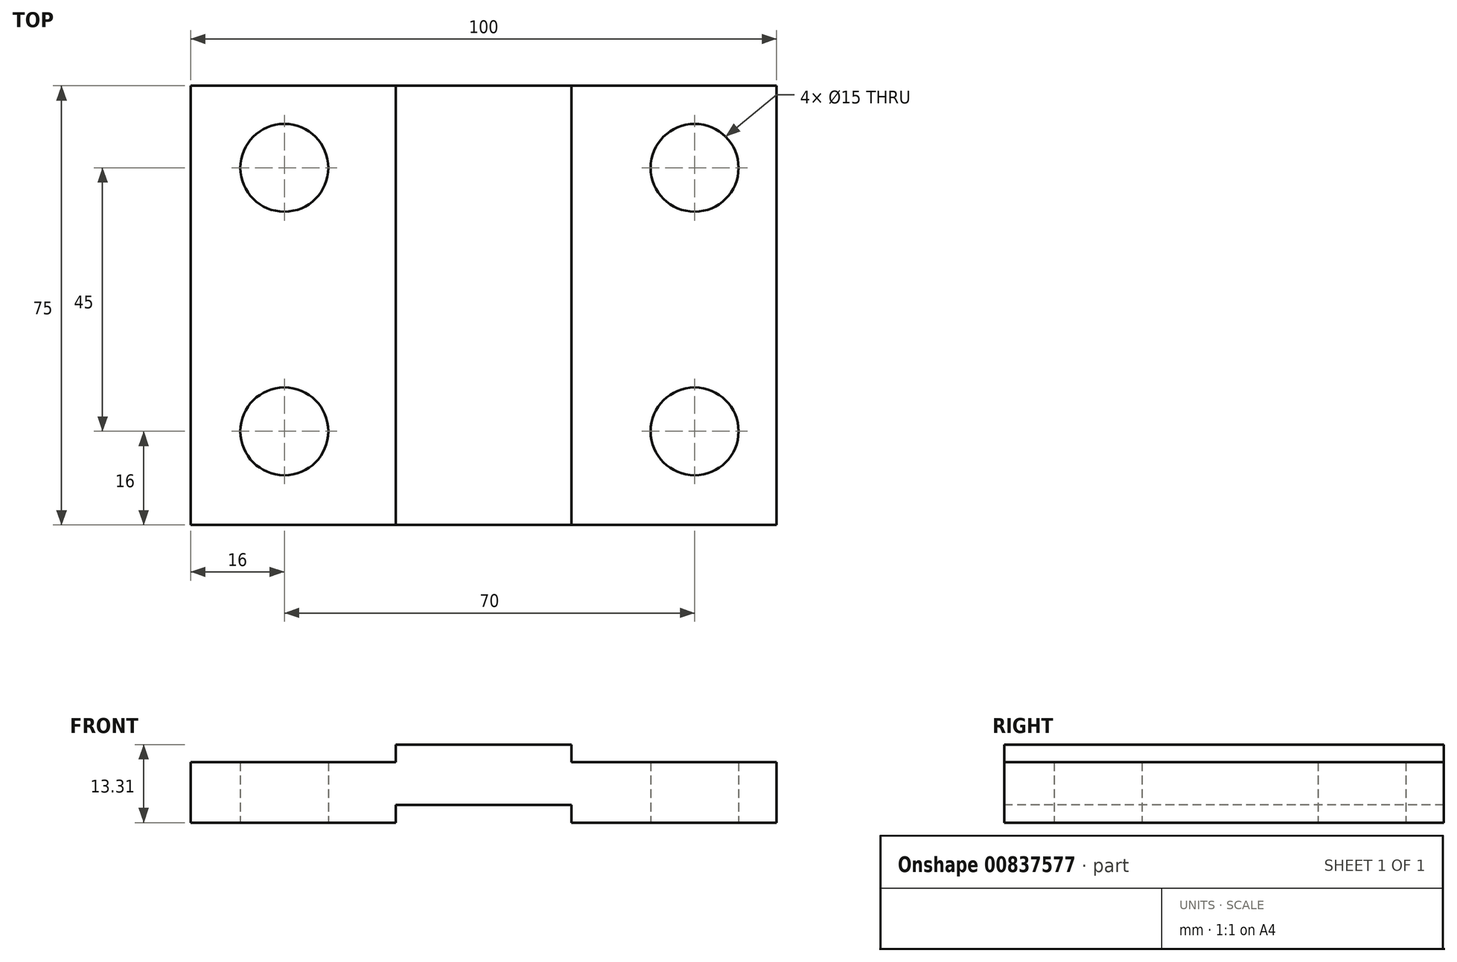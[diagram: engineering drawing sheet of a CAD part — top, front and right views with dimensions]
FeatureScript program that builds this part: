
annotation { "Feature Type Name" : "Feature", "Feature Type Description" : "" }
export const myFeature = defineFeature(function(context is Context, id is Id, definition is map)
    precondition{}
    {
        {
            var Q0;
            Q0=qCreatedBy(makeId("Front.planeOp"),FACE);
            var sketch = newSketch(context, id + "F0", { "sketchPlane" : qUnion([Q0])});
            skLineSegment(sketch, "E0", {"start": v(0, 0) * mm, "end": v(-50, 0) * mm});
            skLineSegment(sketch, "E1.MirrorCS", {"start": v(0, 0) * mm, "end": v(50, 0) * mm});
            skLineSegment(sketch, "E2", {"start": v(-50, 0) * mm, "end": v(-50, 10.3) * mm});
            skLineSegment(sketch, "E3", {"start": v(-50, 10.3) * mm, "end": v(50, 10.31) * mm});
            skLineSegment(sketch, "E4", {"start": v(50, 10.31) * mm, "end": v(50, 0) * mm});
            skSolve(sketch);
        }
        {
            var Q0;
            Q0=makeQuery(id+"F0.imprint","IMPRINT",FACE,{"disambiguationData":[TD([[makeQuery(id+"F0.imprint","IMPRINT",EDGE,{"derivedFrom":sQuery(id+"F0.wireOp",EDGE,"E0")}),-1.0]])]});
            extrude(context, id + "F1", {"entities" : qUnion([Q0]), "oppositeDirection" : true, "depth" : 75 * mm, "offsetDistance" : 25 * mm});
        }
        {
            var Q0;
            Q0=makeQuery(id+"F1.opExtrude","CAP_FACE",FACE,{"disambiguationData":[OSD([sQuery(id+"F0.wireOp",EDGE,"E0"),sQuery(id+"F0.wireOp",EDGE,"E1.MirrorCS"),sQuery(id+"F0.wireOp",EDGE,"E2"),sQuery(id+"F0.wireOp",EDGE,"E3"),sQuery(id+"F0.wireOp",EDGE,"E4")])],"isStart":true});
            cPlane(context, id + "F2", {"entities" : qUnion([Q0]), "cplaneType" : CPlaneType.OFFSET, "offset" : 0 * mm, "width" : 150 * mm, "height" : 150 * mm});
        }
        {
            var Q0;
            Q0=qCreatedBy(id+"F2.planeOp",FACE);
            var sketch = newSketch(context, id + "F3", { "sketchPlane" : qUnion([Q0])});
            skLineSegment(sketch, "E5", {"start": v(0, 0) * mm, "end": v(-15, 0) * mm});
            skLineSegment(sketch, "E6.MirrorCS", {"start": v(0, 0) * mm, "end": v(15, 0) * mm});
            skLineSegment(sketch, "E7", {"start": v(-15, 0) * mm, "end": v(-15, 3) * mm});
            skLineSegment(sketch, "E8", {"start": v(-15, 3) * mm, "end": v(15, 3) * mm});
            skLineSegment(sketch, "E9", {"start": v(15, 3) * mm, "end": v(15, 0) * mm});
            skSolve(sketch);
        }
        {
            var Q0;
            Q0=makeQuery(id+"F3.imprint","IMPRINT",FACE,{"disambiguationData":[TD([[makeQuery(id+"F3.imprint","IMPRINT",EDGE,{"derivedFrom":sQuery(id+"F3.wireOp",EDGE,"E5")}),-1.0]])]});
            extrude(context, id + "F4", {"entities" : qUnion([Q0]), "operationType" : NewBodyOperationType.REMOVE, "endBound" : BoundingType.THROUGH_ALL, "oppositeDirection" : true, "depth" : 25 * mm, "offsetDistance" : 25 * mm});
        }
        {
            var Q0;
            Q0=qCreatedBy(id+"F2.planeOp",FACE);
            cPlane(context, id + "F5", {"entities" : qUnion([Q0]), "cplaneType" : CPlaneType.OFFSET, "offset" : 0 * mm, "width" : 150 * mm, "height" : 150 * mm});
        }
        {
            var Q0;
            Q0=qCreatedBy(id+"F5.planeOp",FACE);
            var sketch = newSketch(context, id + "F6", { "sketchPlane" : qUnion([Q0])});
            skLineSegment(sketch, "E10", {"start": v(0, 10.3) * mm, "end": v(-15, 10.3) * mm});
            skLineSegment(sketch, "E11.MirrorCS", {"start": v(0, 10.3) * mm, "end": v(15, 10.3) * mm});
            skLineSegment(sketch, "E12", {"start": v(-15, 10.3) * mm, "end": v(-15, 13.3) * mm});
            skLineSegment(sketch, "E13", {"start": v(-15, 13.3) * mm, "end": v(15, 13.3) * mm});
            skLineSegment(sketch, "E14", {"start": v(15, 13.3) * mm, "end": v(15, 10.3) * mm});
            skSolve(sketch);
        }
        {
            var Q0;
            Q0=makeQuery(id+"F6.imprint","IMPRINT",FACE,{"disambiguationData":[TD([[makeQuery(id+"F6.imprint","IMPRINT",EDGE,{"derivedFrom":sQuery(id+"F6.wireOp",EDGE,"E10")}),-1.0]])]});
            extrude(context, id + "F7", {"entities" : qUnion([Q0]), "operationType" : NewBodyOperationType.ADD, "oppositeDirection" : true, "depth" : 75 * mm, "offsetDistance" : 25 * mm});
        }
        {
            var Q0;
            Q0=qCreatedBy(makeId("Top.planeOp"),FACE);
            var sketch = newSketch(context, id + "F8", { "sketchPlane" : qUnion([Q0])});
            skCircle(sketch, "E15", {"center": v(-34, 61) * mm, "radius": 7.5 * mm});
            skCircle(sketch, "E16", {"center": v(-34, 16) * mm, "radius": 7.5 * mm});
            skCircle(sketch, "E17", {"center": v(36, 61) * mm, "radius": 7.5 * mm});
            skCircle(sketch, "E18", {"center": v(36, 16) * mm, "radius": 7.5 * mm});
            skSolve(sketch);
        }
        {
            var Q0;
            Q0=sQuery(id+"F8.wireOp",VERTEX,"E15.center");
            var Q1;
            Q1=sQuery(id+"F8.wireOp",VERTEX,"E16.center");
            var Q2;
            Q2=sQuery(id+"F8.wireOp",VERTEX,"E17.center");
            var Q3;
            Q3=sQuery(id+"F8.wireOp",VERTEX,"E18.center");
            var Q4;
            Q4=makeQuery(id+"F1.opExtrude","SWEPT_BODY",BODY,{"disambiguationData":[OSD([sQuery(id+"F0.wireOp",EDGE,"E0"),sQuery(id+"F0.wireOp",EDGE,"E1.MirrorCS"),sQuery(id+"F0.wireOp",EDGE,"E2"),sQuery(id+"F0.wireOp",EDGE,"E3"),sQuery(id+"F0.wireOp",EDGE,"E4")])]});
            hole(context, id + "F9", {"style" : HoleStyle.SIMPLE, "endStyle" : HoleEndStyle.THROUGH, "oppositeDirection" : true, "holeDiameter" : 15 * mm, "majorDiameter" : 5 * mm, "isTappedThrough" : true, "tappedDepth" : 12 * mm, "tapClearance" : 3, "locations" : qUnion([Q0, Q1, Q2, Q3]), "scope" : qUnion([Q4])});
        }
    });
